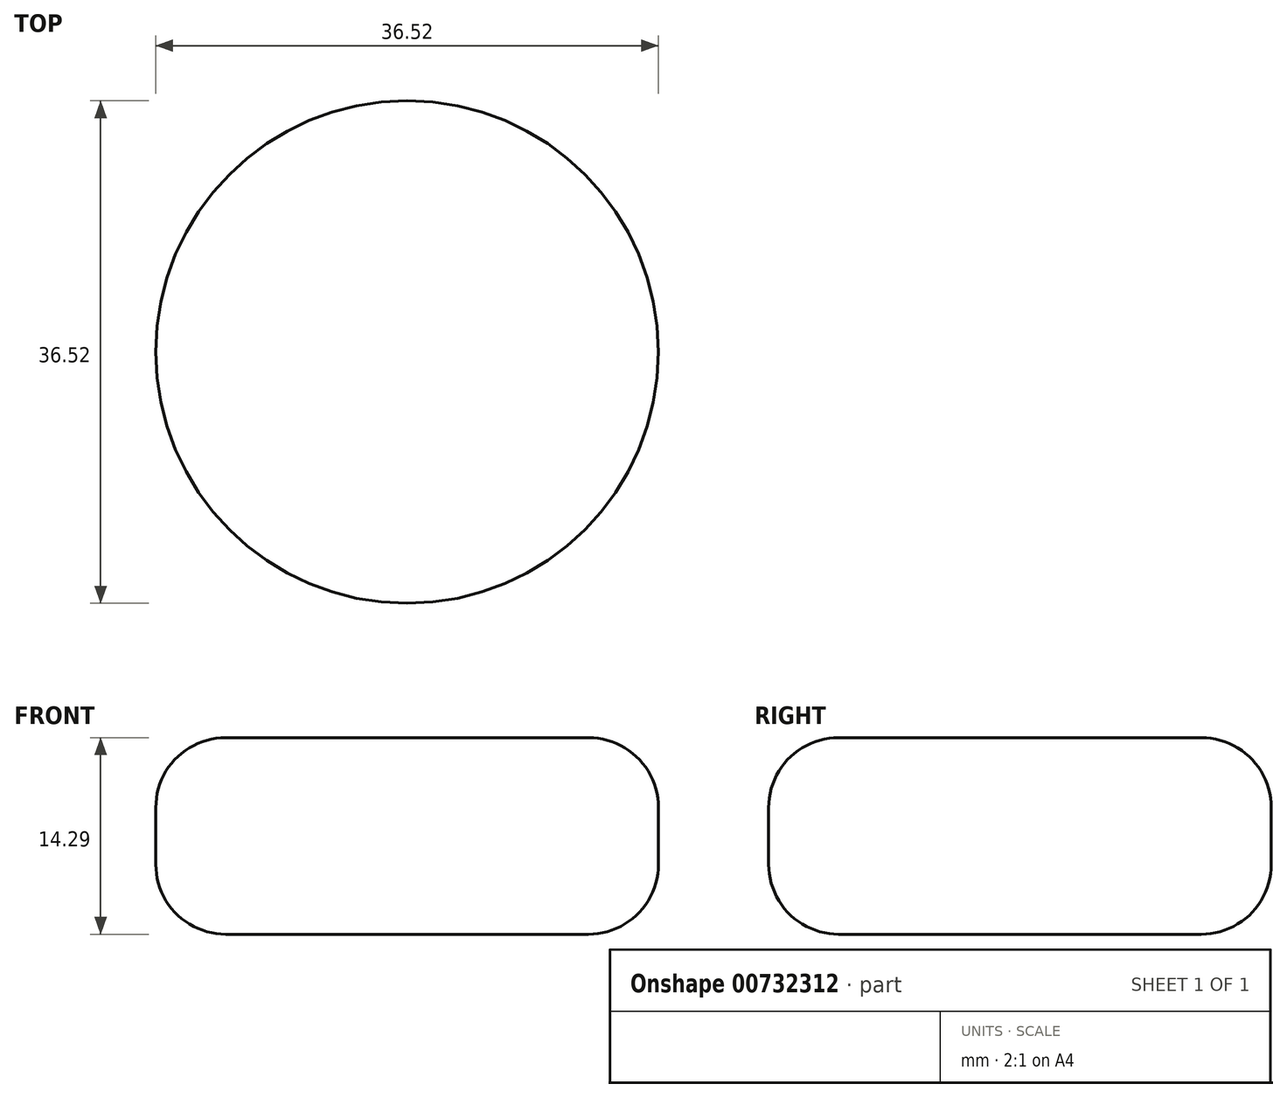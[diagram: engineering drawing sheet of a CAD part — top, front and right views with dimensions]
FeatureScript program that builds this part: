
annotation { "Feature Type Name" : "Feature", "Feature Type Description" : "" }
export const myFeature = defineFeature(function(context is Context, id is Id, definition is map)
    precondition{}
    {
        {
            var Q0;
            Q0=qCreatedBy(makeId("Top.planeOp"),FACE);
            var sketch = newSketch(context, id + "F0", { "sketchPlane" : qUnion([Q0])});
            skCircle(sketch, "E0", {"center": v(0, 0) * mm, "radius": 18.26 * mm});
            skSolve(sketch);
        }
        {
            var Q0;
            Q0=makeQuery(id+"F0.imprint","IMPRINT",FACE,{"disambiguationData":[TD([[makeQuery(id+"F0.imprint","IMPRINT",EDGE,{"derivedFrom":sQuery(id+"F0.wireOp",EDGE,"E0")}),1.0]])]});
            extrude(context, id + "F1", {"entities" : qUnion([Q0]), "depth" : 14.29 * mm, "offsetDistance" : 25.4 * mm});
        }
        {
            var Q0;
            Q0=makeQuery(id+"F1.opExtrude","CAP_FACE",FACE,{"disambiguationData":[OSD([sQuery(id+"F0.wireOp",EDGE,"E0")])],"isStart":false});
            fillet(context, id + "F2", {"entities" : qUnion([Q0]), "radius" : 5.08 * mm, "tangentPropagation" : true, "allowEdgeOverflow" : false});
        }
        {
            var Q0;
            Q0=makeQuery(id+"F1.opExtrude","CAP_FACE",FACE,{"disambiguationData":[OSD([sQuery(id+"F0.wireOp",EDGE,"E0")])],"isStart":true});
            fillet(context, id + "F3", {"entities" : qUnion([Q0]), "radius" : 5.08 * mm, "tangentPropagation" : true, "allowEdgeOverflow" : false});
        }
    });
